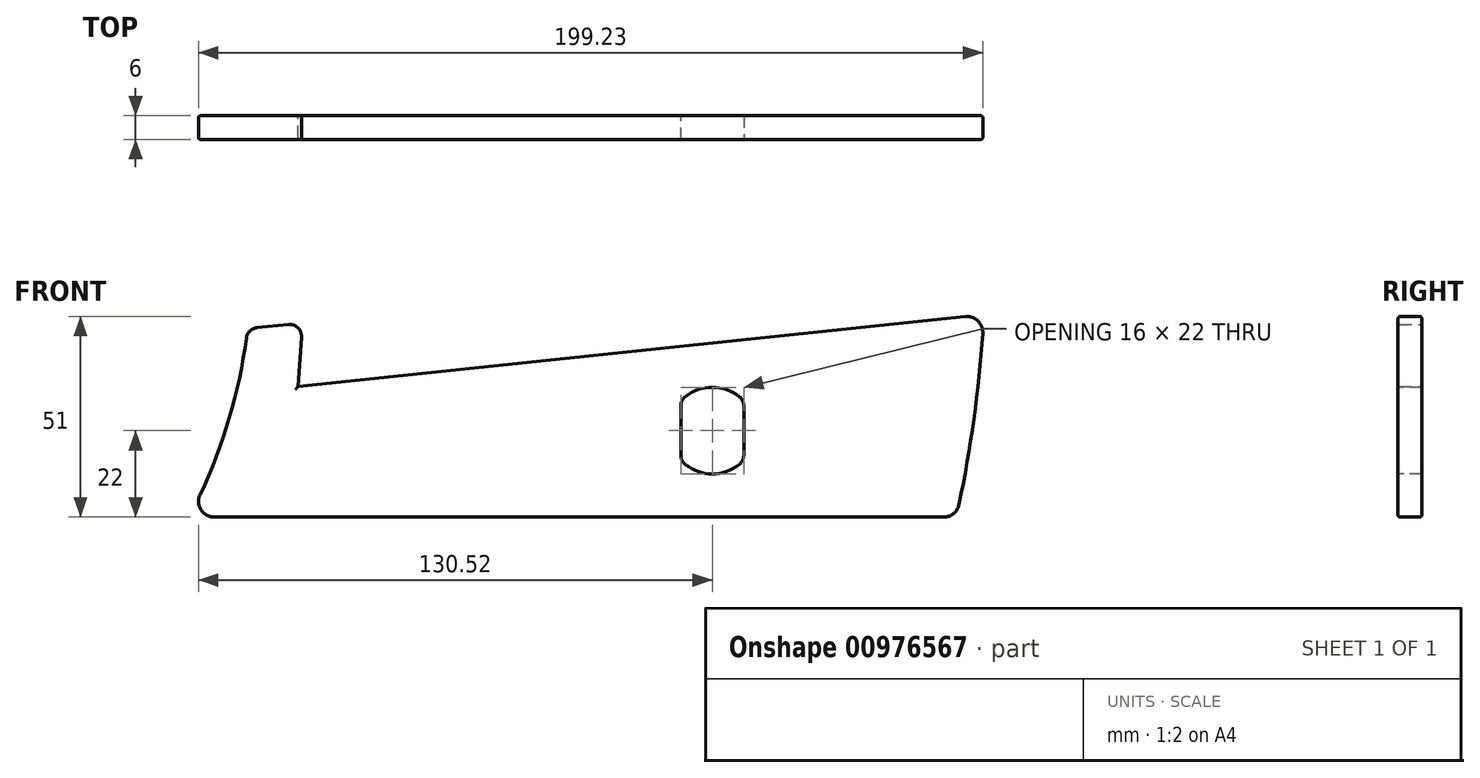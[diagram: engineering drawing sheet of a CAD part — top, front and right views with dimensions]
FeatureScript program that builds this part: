
annotation { "Feature Type Name" : "Feature", "Feature Type Description" : "" }
export const myFeature = defineFeature(function(context is Context, id is Id, definition is map)
    precondition{}
    {
        {
            var Q0;
            Q0=qCreatedBy(makeId("Front.planeOp"),FACE);
            var sketch = newSketch(context, id + "F0", { "sketchPlane" : qUnion([Q0])});
            skLineSegment(sketch, "E0", {"start": v(0, 0) * mm, "end": v(195, 0) * mm});
            skArc(sketch, "E1", {"start": v(0, 0) * mm, "mid": v(6.99, 15.37) * mm, "end": v(12, 31.5) * mm});
            skLineSegment(sketch, "E2", {"start": v(12, 31.5) * mm, "end": v(202, 51.47) * mm});
            skArc(sketch, "E3", {"start": v(195, 0) * mm, "mid": v(199.53, 25.6) * mm, "end": v(202, 51.47) * mm});
            skCircle(sketch, "E4", {"center": v(-119.17, 63.43) * mm, "radius": 135 * mm, "construction": true});
            skSolve(sketch);
        }
        {
            var Q0;
            Q0=makeQuery(id+"F0.imprint","IMPRINT",FACE,{"disambiguationData":[TD([[makeQuery(id+"F0.imprint","IMPRINT",EDGE,{"derivedFrom":sQuery(id+"F0.wireOp",EDGE,"E0")}),1.0]])]});
            extrude(context, id + "F1", {"entities" : qUnion([Q0]), "depth" : 6 * mm, "offsetDistance" : 25 * mm});
        }
        {
            var Q0;
            Q0=makeQuery(id+"F1.opExtrude","SWEPT_EDGE",EDGE,{"disambiguationData":[OSD([sQuery(id+"F0.wireOp",EDGE,"E0"),sQuery(id+"F0.wireOp",EDGE,"E1")])]});
            var Q1;
            Q1=makeQuery(id+"F1.opExtrude","SWEPT_EDGE",EDGE,{"disambiguationData":[OSD([sQuery(id+"F0.wireOp",EDGE,"E0"),sQuery(id+"F0.wireOp",EDGE,"E3")])]});
            var Q2;
            Q2=makeQuery(id+"F1.opExtrude","SWEPT_EDGE",EDGE,{"disambiguationData":[OSD([sQuery(id+"F0.wireOp",EDGE,"E2"),sQuery(id+"F0.wireOp",EDGE,"E3")])]});
            fillet(context, id + "F2", {"entities" : qUnion([Q0, Q1, Q2]), "radius" : 4 * mm, "tangentPropagation" : true, "allowEdgeOverflow" : false});
        }
        {
            var Q0;
            Q0=qCreatedBy(makeId("Front.planeOp"),FACE);
            var sketch = newSketch(context, id + "F3", { "sketchPlane" : qUnion([Q0])});
            skArc(sketch, "E5", {"start": v(12, 31.5) * mm, "mid": v(13.72, 39.65) * mm, "end": v(14.93, 47.9) * mm});
            skLineSegment(sketch, "E6", {"start": v(14.93, 47.9) * mm, "end": v(28.86, 49.36) * mm});
            skLineSegment(sketch, "E7", {"start": v(28.86, 49.36) * mm, "end": v(27.72, 33.15) * mm});
            skLineSegment(sketch, "E8", {"start": v(27.72, 33.15) * mm, "end": v(12, 31.5) * mm});
            skSolve(sketch);
        }
        {
            var Q0;
            Q0=makeQuery(id+"F3.imprint","IMPRINT",FACE,{"disambiguationData":[TD([[makeQuery(id+"F3.imprint","IMPRINT",EDGE,{"derivedFrom":sQuery(id+"F3.wireOp",EDGE,"E5")}),-1.0]])]});
            extrude(context, id + "F4", {"entities" : qUnion([Q0]), "operationType" : NewBodyOperationType.ADD, "depth" : 6 * mm, "offsetDistance" : 25 * mm});
        }
        {
            var Q0;
            Q0=makeQuery(id+"F4.boolean.opBoolean","MERGE",FACE,{"derivedFrom":[makeQuery(id+"F1.opExtrude","CAP_FACE",FACE,{"disambiguationData":[OSD([sQuery(id+"F0.wireOp",EDGE,"E0"),sQuery(id+"F0.wireOp",EDGE,"E1"),sQuery(id+"F0.wireOp",EDGE,"E2"),sQuery(id+"F0.wireOp",EDGE,"E3")])],"isStart":false}),makeQuery(id+"F4.opExtrude","CAP_FACE",FACE,{"disambiguationData":[OSD([sQuery(id+"F3.wireOp",EDGE,"E5"),sQuery(id+"F3.wireOp",EDGE,"E6"),sQuery(id+"F3.wireOp",EDGE,"E7"),sQuery(id+"F3.wireOp",EDGE,"E8")])],"isStart":false})]});
            var sketch = newSketch(context, id + "F5", { "sketchPlane" : qUnion([Q0])});
            skPoint(sketch, "E9", {"position": v(133, 22) * mm});
            skArc(sketch, "E10", {"start": v(141, 29.55) * mm, "mid": v(133, 33) * mm, "end": v(125, 29.55) * mm});
            skLineSegment(sketch, "E11", {"start": v(141, 29.55) * mm, "end": v(141, 14.45) * mm});
            skLineSegment(sketch, "E12", {"start": v(125, 29.55) * mm, "end": v(125, 14.45) * mm});
            skArc(sketch, "E13.trimOffspring", {"start": v(125, 14.45) * mm, "mid": v(133, 11) * mm, "end": v(141, 14.45) * mm});
            skSolve(sketch);
        }
        {
            var Q0;
            Q0 = qSketchRegion(id + "F5", true);
            extrude(context, id + "F6", {"entities" : qUnion([Q0]), "operationType" : NewBodyOperationType.REMOVE, "endBound" : BoundingType.THROUGH_ALL, "oppositeDirection" : true, "depth" : 25 * mm, "offsetDistance" : 25 * mm});
        }
        {
            var Q0;
            Q0=makeQuery(id+"F4.opExtrude","SWEPT_EDGE",EDGE,{"disambiguationData":[OSD([sQuery(id+"F3.wireOp",EDGE,"E5"),sQuery(id+"F3.wireOp",EDGE,"E6")])]});
            var Q1;
            Q1=makeQuery(id+"F4.opExtrude","SWEPT_EDGE",EDGE,{"disambiguationData":[OSD([sQuery(id+"F3.wireOp",EDGE,"E6"),sQuery(id+"F3.wireOp",EDGE,"E7")])]});
            var Q2;
            Q2=makeQuery(id+"F4.opExtrude","SWEPT_EDGE",EDGE,{"disambiguationData":[OSD([sQuery(id+"F3.wireOp",EDGE,"E7"),sQuery(id+"F3.wireOp",EDGE,"E8")])]});
            var Q3;
            Q3=makeQuery(id+"F6.boolean.opBoolean","COPY",EDGE,{"derivedFrom":makeQuery(id+"F6.opExtrude","SWEPT_EDGE",EDGE,{"disambiguationData":[OSD([sQuery(id+"F5.wireOp",EDGE,"E12"),sQuery(id+"F5.wireOp",EDGE,"E13.trimOffspring")])]})});
            var Q4;
            Q4=makeQuery(id+"F6.boolean.opBoolean","COPY",EDGE,{"derivedFrom":makeQuery(id+"F6.opExtrude","SWEPT_EDGE",EDGE,{"disambiguationData":[OSD([sQuery(id+"F5.wireOp",EDGE,"E10"),sQuery(id+"F5.wireOp",EDGE,"E12")])]})});
            var Q5;
            Q5=makeQuery(id+"F6.boolean.opBoolean","COPY",EDGE,{"derivedFrom":makeQuery(id+"F6.opExtrude","SWEPT_EDGE",EDGE,{"disambiguationData":[OSD([sQuery(id+"F5.wireOp",EDGE,"E10"),sQuery(id+"F5.wireOp",EDGE,"E11")])]})});
            var Q6;
            Q6=makeQuery(id+"F6.boolean.opBoolean","COPY",EDGE,{"derivedFrom":makeQuery(id+"F6.opExtrude","SWEPT_EDGE",EDGE,{"disambiguationData":[OSD([sQuery(id+"F5.wireOp",EDGE,"E11"),sQuery(id+"F5.wireOp",EDGE,"E13.trimOffspring")])]})});
            fillet(context, id + "F7", {"entities" : qUnion([Q0, Q1, Q2, Q3, Q4, Q5, Q6]), "radius" : 3 * mm, "tangentPropagation" : true, "defaultsChanged" : false, "vertexSettings" : [], "allowEdgeOverflow" : false});
        }
        {
            var Q0;
            Q0=makeQuery(id+"F4.boolean.opBoolean","MERGE",EDGE,{"derivedFrom":[makeQuery(id+"F1.opExtrude","CAP_EDGE",EDGE,{"disambiguationData":[OSD([sQuery(id+"F0.wireOp",EDGE,"E1")])],"isStart":false}),makeQuery(id+"F4.opExtrude","CAP_EDGE",EDGE,{"disambiguationData":[OSD([sQuery(id+"F3.wireOp",EDGE,"E5")])],"isStart":false})]});
            var Q1;
            Q1=makeQuery(id+"F4.boolean.opBoolean","MERGE",EDGE,{"derivedFrom":[makeQuery(id+"F1.opExtrude","CAP_EDGE",EDGE,{"disambiguationData":[OSD([sQuery(id+"F0.wireOp",EDGE,"E1")])],"isStart":true}),makeQuery(id+"F4.opExtrude","CAP_EDGE",EDGE,{"disambiguationData":[OSD([sQuery(id+"F3.wireOp",EDGE,"E5")])],"isStart":true})]});
            fillet(context, id + "F8", {"entities" : qUnion([Q0, Q1]), "radius" : 0.5 * mm, "tangentPropagation" : true, "defaultsChanged" : true, "vertexSettings" : [], "allowEdgeOverflow" : false});
        }
    });
